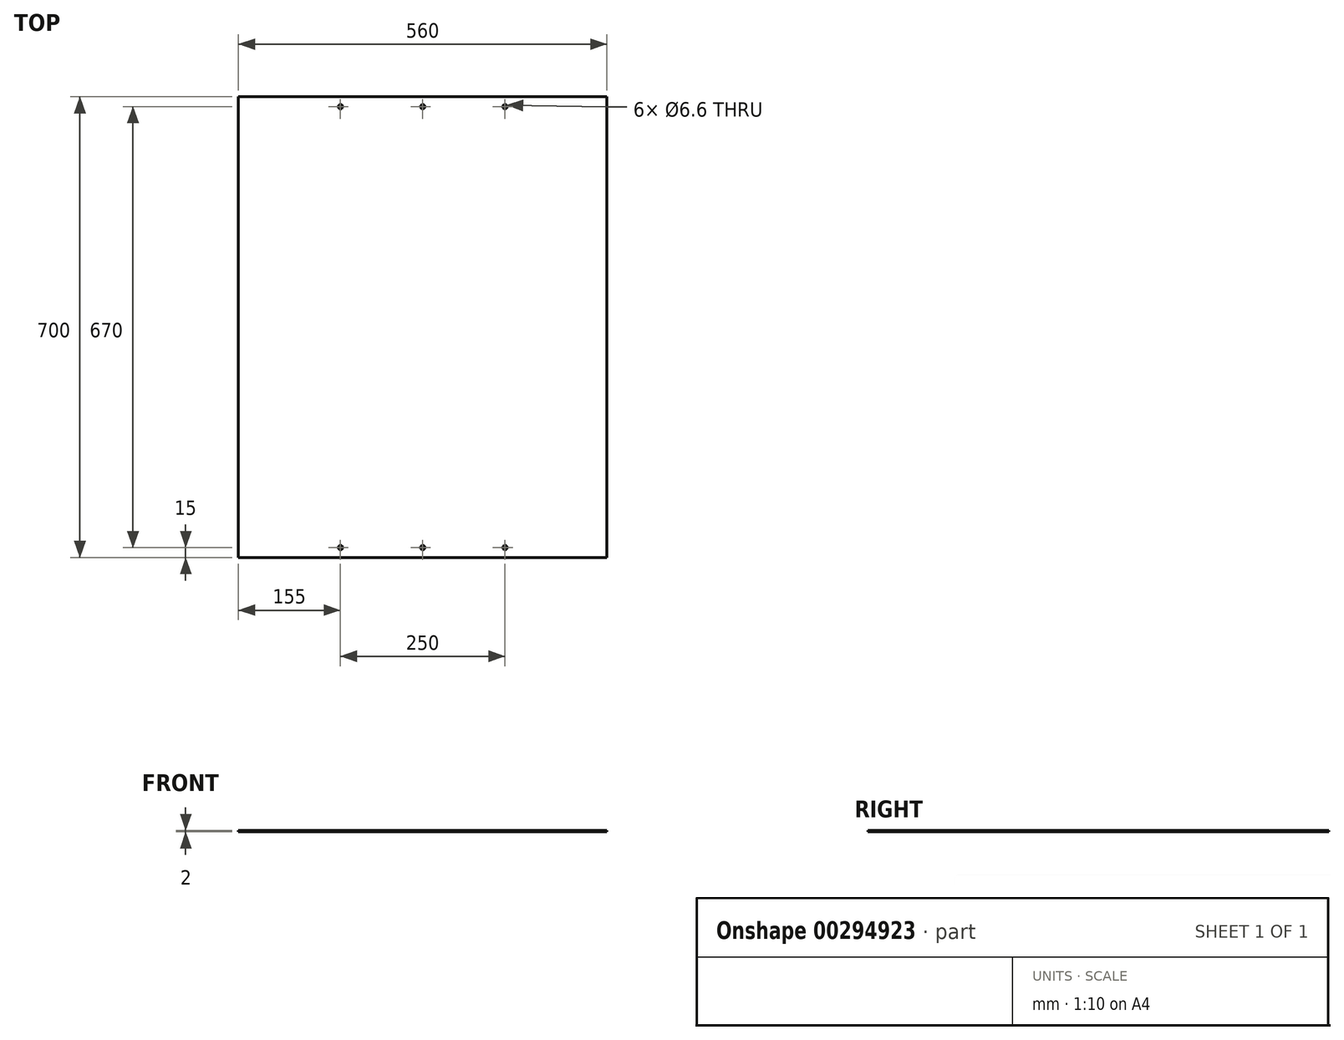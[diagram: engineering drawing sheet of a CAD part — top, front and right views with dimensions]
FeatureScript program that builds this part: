
annotation { "Feature Type Name" : "Feature", "Feature Type Description" : "" }
export const myFeature = defineFeature(function(context is Context, id is Id, definition is map)
    precondition{}
    {
        {
            var Q0;
            Q0=qCreatedBy(makeId("Top.planeOp"),FACE);
            var sketch = newSketch(context, id + "F0", { "sketchPlane" : qUnion([Q0])});
            skLineSegment(sketch, "E0.bottom", {"start": v(280, 350) * mm, "end": v(-280, 350) * mm});
            skLineSegment(sketch, "E0.top", {"start": v(280, -350) * mm, "end": v(-280, -350) * mm});
            skLineSegment(sketch, "E0.left", {"start": v(280, 350) * mm, "end": v(280, -350) * mm});
            skLineSegment(sketch, "E0.right", {"start": v(-280, 350) * mm, "end": v(-280, -350) * mm});
            skPoint(sketch, "E0.middle", {"position": v(0, 0) * mm});
            skSolve(sketch);
        }
        {
            var Q0;
            Q0=makeQuery(id+"F0.imprint","IMPRINT",FACE,{"disambiguationData":[TD([[makeQuery(id+"F0.imprint","IMPRINT",EDGE,{"derivedFrom":sQuery(id+"F0.wireOp",EDGE,"E0.bottom")}),1.0]])]});
            extrude(context, id + "F1", {"entities" : qUnion([Q0]), "depth" : 2 * mm, "offsetDistance" : 25 * mm});
        }
        {
            var Q0;
            Q0=makeQuery(id+"F1.opExtrude","CAP_FACE",FACE,{"disambiguationData":[OSD([sQuery(id+"F0.wireOp",EDGE,"E0.bottom"),sQuery(id+"F0.wireOp",EDGE,"E0.top"),sQuery(id+"F0.wireOp",EDGE,"E0.left"),sQuery(id+"F0.wireOp",EDGE,"E0.right")])],"isStart":false});
            var sketch = newSketch(context, id + "F2", { "sketchPlane" : qUnion([Q0])});
            skLineSegment(sketch, "E1", {"start": v(-280, 335) * mm, "end": v(280, 335) * mm, "construction": true});
            skLineSegment(sketch, "E2", {"start": v(-280, -335) * mm, "end": v(280, -335) * mm, "construction": true});
            skLineSegment(sketch, "E3", {"start": v(-250, 350) * mm, "end": v(-250, -350) * mm, "construction": true});
            skLineSegment(sketch, "E4", {"start": v(250, 350) * mm, "end": v(250, -350) * mm, "construction": true});
            skPoint(sketch, "E5", {"position": v(-125, 335) * mm});
            skPoint(sketch, "E6", {"position": v(0, 335) * mm});
            skPoint(sketch, "E7", {"position": v(125, 335) * mm});
            skPoint(sketch, "E8", {"position": v(-125, -335) * mm});
            skPoint(sketch, "E9", {"position": v(0, -335) * mm});
            skPoint(sketch, "E10", {"position": v(125, -335) * mm});
            skSolve(sketch);
        }
        {
            var Q0;
            Q0=sQuery(id+"F2.wireOp",VERTEX,"E5");
            var Q1;
            Q1=sQuery(id+"F2.wireOp",VERTEX,"E6");
            var Q2;
            Q2=sQuery(id+"F2.wireOp",VERTEX,"E7");
            var Q3;
            Q3=sQuery(id+"F2.wireOp",VERTEX,"E10");
            var Q4;
            Q4=sQuery(id+"F2.wireOp",VERTEX,"E9");
            var Q5;
            Q5=sQuery(id+"F2.wireOp",VERTEX,"E8");
            var Q6;
            Q6=makeQuery(id+"F1.opExtrude","SWEPT_BODY",BODY,{"disambiguationData":[OSD([sQuery(id+"F0.wireOp",EDGE,"E0.bottom"),sQuery(id+"F0.wireOp",EDGE,"E0.top"),sQuery(id+"F0.wireOp",EDGE,"E0.left"),sQuery(id+"F0.wireOp",EDGE,"E0.right")])]});
            hole(context, id + "F3", {"style" : HoleStyle.SIMPLE, "endStyle" : HoleEndStyle.THROUGH, "standardTappedOrClearance" : lookupTablePath({ "standard" : "ISO", "fit" : "Normal", "size" : "M6", "type" : "Clearance" }), "standardBlindInLast" : lookupTablePath({ "fit" : "Standard", "standard" : "ISO", "size" : "M6", "type" : "Clearance" }), "holeDiameter" : 6.6 * mm, "isTappedThrough" : true, "tappedDepth" : 12 * mm, "tapClearance" : 3, "locations" : qUnion([Q0, Q1, Q2, Q3, Q4, Q5]), "scope" : qUnion([Q6])});
        }
    });
